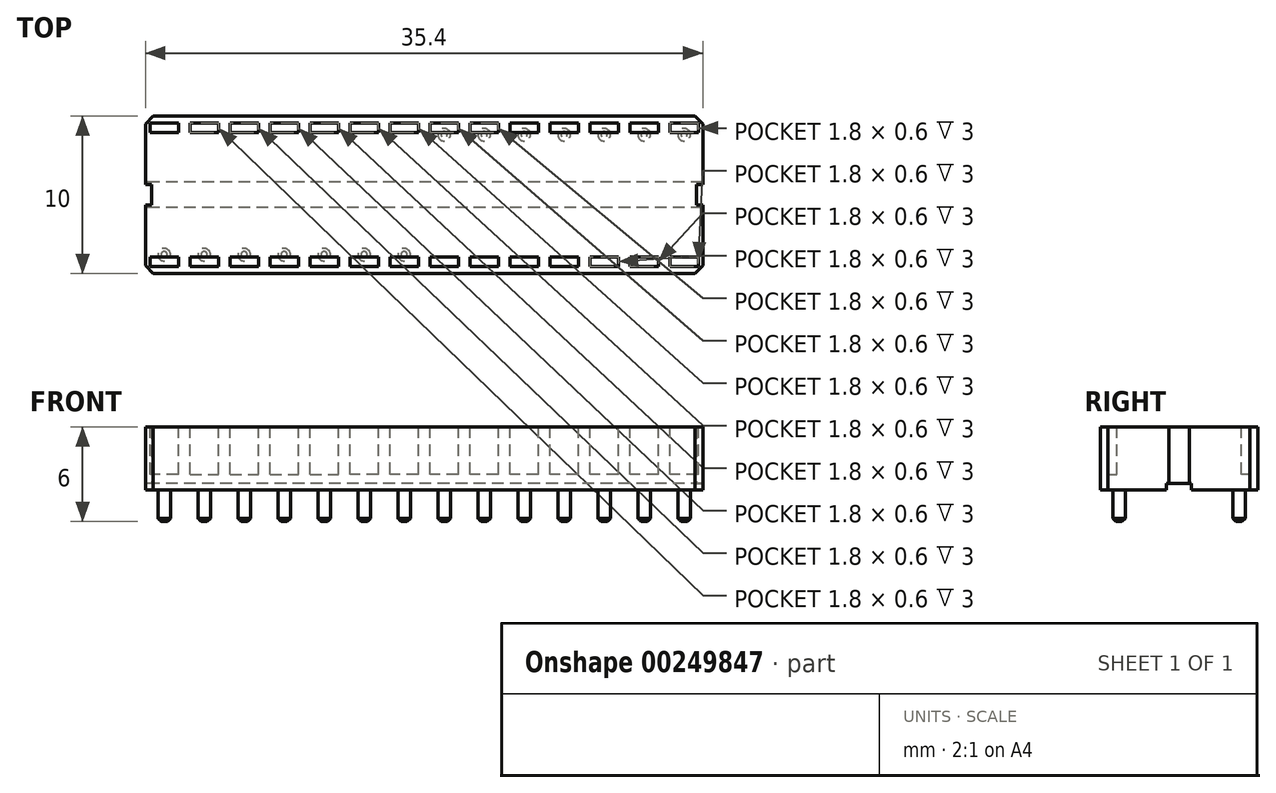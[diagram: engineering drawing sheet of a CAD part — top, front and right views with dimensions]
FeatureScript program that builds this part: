
annotation { "Feature Type Name" : "Feature", "Feature Type Description" : "" }
export const myFeature = defineFeature(function(context is Context, id is Id, definition is map)
    precondition{}
    {
        {
            var Q0;
            Q0=qCreatedBy(makeId("Top.planeOp"),FACE);
            var sketch = newSketch(context, id + "F0", { "sketchPlane" : qUnion([Q0])});
            skLineSegment(sketch, "E0.bottom", {"start": v(0, 0) * mm, "end": v(35.4, 0) * mm});
            skLineSegment(sketch, "E0.top", {"start": v(0, 10) * mm, "end": v(35.4, 10) * mm});
            skLineSegment(sketch, "E0.left", {"start": v(0, 0) * mm, "end": v(0, 10) * mm});
            skLineSegment(sketch, "E0.right", {"start": v(35.4, 0) * mm, "end": v(35.4, 10) * mm});
            skSolve(sketch);
        }
        {
            var Q0;
            Q0=makeQuery(id+"F0.imprint","IMPRINT",FACE,{"disambiguationData":[TD([[makeQuery(id+"F0.imprint","IMPRINT",EDGE,{"derivedFrom":sQuery(id+"F0.wireOp",EDGE,"E0.bottom")}),1.0]])]});
            extrude(context, id + "F1", {"entities" : qUnion([Q0]), "depth" : 8.6 * mm});
        }
        {
            var Q0;
            Q0=makeQuery(id+"F1.opExtrude","CAP_FACE",FACE,{"disambiguationData":[OSD([sQuery(id+"F0.wireOp",EDGE,"E0.bottom"),sQuery(id+"F0.wireOp",EDGE,"E0.top"),sQuery(id+"F0.wireOp",EDGE,"E0.left"),sQuery(id+"F0.wireOp",EDGE,"E0.right")])],"isStart":true});
            var sketch = newSketch(context, id + "F2", { "sketchPlane" : qUnion([Q0])});
            skLineSegment(sketch, "E1", {"start": v(0, -5) * mm, "end": v(35.4, -5) * mm, "construction": true});
            skLineSegment(sketch, "E2", {"start": v(17.7, 0) * mm, "end": v(17.7, -10) * mm, "construction": true});
            skLineSegment(sketch, "E3", {"start": v(0, -1.19) * mm, "end": v(35.4, -1.19) * mm, "construction": true});
            skCircle(sketch, "E4", {"center": v(16.43, -1.19) * mm, "radius": 0.4 * mm});
            skCircle(sketch, "E5.1.0.0", {"center": v(13.89, -1.19) * mm, "radius": 0.4 * mm});
            skCircle(sketch, "E5.2.0.0", {"center": v(11.35, -1.19) * mm, "radius": 0.4 * mm});
            skCircle(sketch, "E5.3.0.0", {"center": v(8.8, -1.19) * mm, "radius": 0.4 * mm});
            skCircle(sketch, "E5.4.0.0", {"center": v(6.27, -1.19) * mm, "radius": 0.4 * mm});
            skCircle(sketch, "E5.5.0.0", {"center": v(3.73, -1.19) * mm, "radius": 0.4 * mm});
            skCircle(sketch, "E5.6.0.0", {"center": v(1.19, -1.19) * mm, "radius": 0.4 * mm});
            skLineSegment(sketch, "E5.direction1", {"start": v(16.43, -1.19) * mm, "end": v(13.89, -1.19) * mm, "construction": true});
            skCircle(sketch, "E6.MirrorC", {"center": v(1.19, -8.8) * mm, "radius": 0.4 * mm});
            skCircle(sketch, "E7.MirrorC", {"center": v(3.73, -8.8) * mm, "radius": 0.4 * mm});
            skCircle(sketch, "E8.MirrorC", {"center": v(6.27, -8.8) * mm, "radius": 0.4 * mm});
            skCircle(sketch, "E9.MirrorC", {"center": v(8.8, -8.8) * mm, "radius": 0.4 * mm});
            skCircle(sketch, "E10.MirrorC", {"center": v(11.35, -8.8) * mm, "radius": 0.4 * mm});
            skCircle(sketch, "E11.MirrorC", {"center": v(13.89, -8.8) * mm, "radius": 0.4 * mm});
            skCircle(sketch, "E12.MirrorC", {"center": v(16.43, -8.8) * mm, "radius": 0.4 * mm});
            skCircle(sketch, "E13.MirrorC", {"center": v(34.2, -1.19) * mm, "radius": 0.4 * mm});
            skCircle(sketch, "E14.MirrorC", {"center": v(31.67, -1.19) * mm, "radius": 0.4 * mm});
            skCircle(sketch, "E15.MirrorC", {"center": v(29.13, -1.19) * mm, "radius": 0.4 * mm});
            skCircle(sketch, "E16.MirrorC", {"center": v(26.6, -1.19) * mm, "radius": 0.4 * mm});
            skCircle(sketch, "E17.MirrorC", {"center": v(24.05, -1.19) * mm, "radius": 0.4 * mm});
            skCircle(sketch, "E18.MirrorC", {"center": v(21.51, -1.19) * mm, "radius": 0.4 * mm});
            skCircle(sketch, "E19.MirrorC", {"center": v(18.97, -1.19) * mm, "radius": 0.4 * mm});
            skCircle(sketch, "E20.MirrorC", {"center": v(18.97, -8.8) * mm, "radius": 0.4 * mm});
            skCircle(sketch, "E21.MirrorC", {"center": v(21.51, -8.8) * mm, "radius": 0.4 * mm});
            skCircle(sketch, "E22.MirrorC", {"center": v(24.05, -8.8) * mm, "radius": 0.4 * mm});
            skCircle(sketch, "E23.MirrorC", {"center": v(26.6, -8.8) * mm, "radius": 0.4 * mm});
            skCircle(sketch, "E24.MirrorC", {"center": v(29.13, -8.8) * mm, "radius": 0.4 * mm});
            skCircle(sketch, "E25.MirrorC", {"center": v(31.67, -8.8) * mm, "radius": 0.4 * mm});
            skCircle(sketch, "E26.MirrorC", {"center": v(34.2, -8.8) * mm, "radius": 0.4 * mm});
            skSolve(sketch);
        }
        {
            var Q0;
            Q0=makeQuery(id+"F2.imprint","IMPRINT",FACE,{"disambiguationData":[TD([[makeQuery(id+"F2.imprint","IMPRINT",EDGE,{"derivedFrom":sQuery(id+"F2.wireOp",EDGE,"E8.MirrorC")}),-1.0]])]});
            var Q1;
            Q1=makeQuery(id+"F2.imprint","IMPRINT",FACE,{"disambiguationData":[TD([[makeQuery(id+"F2.imprint","IMPRINT",EDGE,{"derivedFrom":sQuery(id+"F2.wireOp",EDGE,"E7.MirrorC")}),-1.0]])]});
            var Q2;
            Q2=makeQuery(id+"F2.imprint","IMPRINT",FACE,{"disambiguationData":[TD([[makeQuery(id+"F2.imprint","IMPRINT",EDGE,{"derivedFrom":sQuery(id+"F2.wireOp",EDGE,"E6.MirrorC")}),-1.0]])]});
            var Q3;
            Q3=makeQuery(id+"F2.imprint","IMPRINT",FACE,{"disambiguationData":[TD([[makeQuery(id+"F2.imprint","IMPRINT",EDGE,{"derivedFrom":sQuery(id+"F2.wireOp",EDGE,"E5.6.0.0")}),1.0]])]});
            var Q4;
            Q4=makeQuery(id+"F2.imprint","IMPRINT",FACE,{"disambiguationData":[TD([[makeQuery(id+"F2.imprint","IMPRINT",EDGE,{"derivedFrom":sQuery(id+"F2.wireOp",EDGE,"E5.5.0.0")}),1.0]])]});
            var Q5;
            Q5=makeQuery(id+"F2.imprint","IMPRINT",FACE,{"disambiguationData":[TD([[makeQuery(id+"F2.imprint","IMPRINT",EDGE,{"derivedFrom":sQuery(id+"F2.wireOp",EDGE,"E5.4.0.0")}),1.0]])]});
            var Q6;
            Q6=makeQuery(id+"F2.imprint","IMPRINT",FACE,{"disambiguationData":[TD([[makeQuery(id+"F2.imprint","IMPRINT",EDGE,{"derivedFrom":sQuery(id+"F2.wireOp",EDGE,"E5.3.0.0")}),1.0]])]});
            var Q7;
            Q7=makeQuery(id+"F2.imprint","IMPRINT",FACE,{"disambiguationData":[TD([[makeQuery(id+"F2.imprint","IMPRINT",EDGE,{"derivedFrom":sQuery(id+"F2.wireOp",EDGE,"E9.MirrorC")}),-1.0]])]});
            var Q8;
            Q8=makeQuery(id+"F2.imprint","IMPRINT",FACE,{"disambiguationData":[TD([[makeQuery(id+"F2.imprint","IMPRINT",EDGE,{"derivedFrom":sQuery(id+"F2.wireOp",EDGE,"E5.2.0.0")}),1.0]])]});
            var Q9;
            Q9=makeQuery(id+"F2.imprint","IMPRINT",FACE,{"disambiguationData":[TD([[makeQuery(id+"F2.imprint","IMPRINT",EDGE,{"derivedFrom":sQuery(id+"F2.wireOp",EDGE,"E5.1.0.0")}),1.0]])]});
            var Q10;
            Q10=makeQuery(id+"F2.imprint","IMPRINT",FACE,{"disambiguationData":[TD([[makeQuery(id+"F2.imprint","IMPRINT",EDGE,{"derivedFrom":sQuery(id+"F2.wireOp",EDGE,"E10.MirrorC")}),-1.0]])]});
            var Q11;
            Q11=makeQuery(id+"F2.imprint","IMPRINT",FACE,{"disambiguationData":[TD([[makeQuery(id+"F2.imprint","IMPRINT",EDGE,{"derivedFrom":sQuery(id+"F2.wireOp",EDGE,"E11.MirrorC")}),-1.0]])]});
            var Q12;
            Q12=makeQuery(id+"F2.imprint","IMPRINT",FACE,{"disambiguationData":[TD([[makeQuery(id+"F2.imprint","IMPRINT",EDGE,{"derivedFrom":sQuery(id+"F2.wireOp",EDGE,"E4")}),1.0]])]});
            var Q13;
            Q13=makeQuery(id+"F2.imprint","IMPRINT",FACE,{"disambiguationData":[TD([[makeQuery(id+"F2.imprint","IMPRINT",EDGE,{"derivedFrom":sQuery(id+"F2.wireOp",EDGE,"E12.MirrorC")}),-1.0]])]});
            var Q14;
            Q14=makeQuery(id+"F2.imprint","IMPRINT",FACE,{"disambiguationData":[TD([[makeQuery(id+"F2.imprint","IMPRINT",EDGE,{"derivedFrom":sQuery(id+"F2.wireOp",EDGE,"E19.MirrorC")}),-1.0]])]});
            var Q15;
            Q15=makeQuery(id+"F2.imprint","IMPRINT",FACE,{"disambiguationData":[TD([[makeQuery(id+"F2.imprint","IMPRINT",EDGE,{"derivedFrom":sQuery(id+"F2.wireOp",EDGE,"E18.MirrorC")}),-1.0]])]});
            var Q16;
            Q16=makeQuery(id+"F2.imprint","IMPRINT",FACE,{"disambiguationData":[TD([[makeQuery(id+"F2.imprint","IMPRINT",EDGE,{"derivedFrom":sQuery(id+"F2.wireOp",EDGE,"E20.MirrorC")}),1.0]])]});
            var Q17;
            Q17=makeQuery(id+"F2.imprint","IMPRINT",FACE,{"disambiguationData":[TD([[makeQuery(id+"F2.imprint","IMPRINT",EDGE,{"derivedFrom":sQuery(id+"F2.wireOp",EDGE,"E21.MirrorC")}),1.0]])]});
            var Q18;
            Q18=makeQuery(id+"F2.imprint","IMPRINT",FACE,{"disambiguationData":[TD([[makeQuery(id+"F2.imprint","IMPRINT",EDGE,{"derivedFrom":sQuery(id+"F2.wireOp",EDGE,"E22.MirrorC")}),1.0]])]});
            var Q19;
            Q19=makeQuery(id+"F2.imprint","IMPRINT",FACE,{"disambiguationData":[TD([[makeQuery(id+"F2.imprint","IMPRINT",EDGE,{"derivedFrom":sQuery(id+"F2.wireOp",EDGE,"E17.MirrorC")}),-1.0]])]});
            var Q20;
            Q20=makeQuery(id+"F2.imprint","IMPRINT",FACE,{"disambiguationData":[TD([[makeQuery(id+"F2.imprint","IMPRINT",EDGE,{"derivedFrom":sQuery(id+"F2.wireOp",EDGE,"E23.MirrorC")}),1.0]])]});
            var Q21;
            Q21=makeQuery(id+"F2.imprint","IMPRINT",FACE,{"disambiguationData":[TD([[makeQuery(id+"F2.imprint","IMPRINT",EDGE,{"derivedFrom":sQuery(id+"F2.wireOp",EDGE,"E16.MirrorC")}),-1.0]])]});
            var Q22;
            Q22=makeQuery(id+"F2.imprint","IMPRINT",FACE,{"disambiguationData":[TD([[makeQuery(id+"F2.imprint","IMPRINT",EDGE,{"derivedFrom":sQuery(id+"F2.wireOp",EDGE,"E15.MirrorC")}),-1.0]])]});
            var Q23;
            Q23=makeQuery(id+"F2.imprint","IMPRINT",FACE,{"disambiguationData":[TD([[makeQuery(id+"F2.imprint","IMPRINT",EDGE,{"derivedFrom":sQuery(id+"F2.wireOp",EDGE,"E24.MirrorC")}),1.0]])]});
            var Q24;
            Q24=makeQuery(id+"F2.imprint","IMPRINT",FACE,{"disambiguationData":[TD([[makeQuery(id+"F2.imprint","IMPRINT",EDGE,{"derivedFrom":sQuery(id+"F2.wireOp",EDGE,"E14.MirrorC")}),-1.0]])]});
            var Q25;
            Q25=makeQuery(id+"F2.imprint","IMPRINT",FACE,{"disambiguationData":[TD([[makeQuery(id+"F2.imprint","IMPRINT",EDGE,{"derivedFrom":sQuery(id+"F2.wireOp",EDGE,"E25.MirrorC")}),1.0]])]});
            var Q26;
            Q26=makeQuery(id+"F2.imprint","IMPRINT",FACE,{"disambiguationData":[TD([[makeQuery(id+"F2.imprint","IMPRINT",EDGE,{"derivedFrom":sQuery(id+"F2.wireOp",EDGE,"E13.MirrorC")}),-1.0]])]});
            var Q27;
            Q27=makeQuery(id+"F2.imprint","IMPRINT",FACE,{"disambiguationData":[TD([[makeQuery(id+"F2.imprint","IMPRINT",EDGE,{"derivedFrom":sQuery(id+"F2.wireOp",EDGE,"E26.MirrorC")}),1.0]])]});
            extrude(context, id + "F3", {"entities" : qUnion([Q0, Q1, Q2, Q3, Q4, Q5, Q6, Q7, Q8, Q9, Q10, Q11, Q12, Q13, Q14, Q15, Q16, Q17, Q18, Q19, Q20, Q21, Q22, Q23, Q24, Q25, Q26, Q27]), "operationType" : NewBodyOperationType.ADD, "depth" : 2 * mm});
        }
        {
            var Q0;
            Q0=makeQuery(id+"F3.opExtrude","CAP_EDGE",EDGE,{"disambiguationData":[OSD([sQuery(id+"F2.wireOp",EDGE,"E5.6.0.0")])],"isStart":false});
            var Q1;
            Q1=makeQuery(id+"F3.opExtrude","CAP_EDGE",EDGE,{"disambiguationData":[OSD([sQuery(id+"F2.wireOp",EDGE,"E5.5.0.0")])],"isStart":false});
            var Q2;
            Q2=makeQuery(id+"F3.opExtrude","CAP_EDGE",EDGE,{"disambiguationData":[OSD([sQuery(id+"F2.wireOp",EDGE,"E5.4.0.0")])],"isStart":false});
            var Q3;
            Q3=makeQuery(id+"F3.opExtrude","CAP_EDGE",EDGE,{"disambiguationData":[OSD([sQuery(id+"F2.wireOp",EDGE,"E5.3.0.0")])],"isStart":false});
            var Q4;
            Q4=makeQuery(id+"F3.opExtrude","CAP_EDGE",EDGE,{"disambiguationData":[OSD([sQuery(id+"F2.wireOp",EDGE,"E5.2.0.0")])],"isStart":false});
            var Q5;
            Q5=makeQuery(id+"F3.opExtrude","CAP_EDGE",EDGE,{"disambiguationData":[OSD([sQuery(id+"F2.wireOp",EDGE,"E5.1.0.0")])],"isStart":false});
            var Q6;
            Q6=makeQuery(id+"F3.opExtrude","CAP_EDGE",EDGE,{"disambiguationData":[OSD([sQuery(id+"F2.wireOp",EDGE,"E4")])],"isStart":false});
            var Q7;
            Q7=makeQuery(id+"F3.opExtrude","CAP_EDGE",EDGE,{"disambiguationData":[OSD([sQuery(id+"F2.wireOp",EDGE,"E6.MirrorC")])],"isStart":false});
            var Q8;
            Q8=makeQuery(id+"F3.opExtrude","CAP_EDGE",EDGE,{"disambiguationData":[OSD([sQuery(id+"F2.wireOp",EDGE,"E7.MirrorC")])],"isStart":false});
            var Q9;
            Q9=makeQuery(id+"F3.opExtrude","CAP_EDGE",EDGE,{"disambiguationData":[OSD([sQuery(id+"F2.wireOp",EDGE,"E8.MirrorC")])],"isStart":false});
            var Q10;
            Q10=makeQuery(id+"F3.opExtrude","CAP_EDGE",EDGE,{"disambiguationData":[OSD([sQuery(id+"F2.wireOp",EDGE,"E9.MirrorC")])],"isStart":false});
            var Q11;
            Q11=makeQuery(id+"F3.opExtrude","CAP_EDGE",EDGE,{"disambiguationData":[OSD([sQuery(id+"F2.wireOp",EDGE,"E10.MirrorC")])],"isStart":false});
            var Q12;
            Q12=makeQuery(id+"F3.opExtrude","CAP_EDGE",EDGE,{"disambiguationData":[OSD([sQuery(id+"F2.wireOp",EDGE,"E11.MirrorC")])],"isStart":false});
            var Q13;
            Q13=makeQuery(id+"F3.opExtrude","CAP_EDGE",EDGE,{"disambiguationData":[OSD([sQuery(id+"F2.wireOp",EDGE,"E12.MirrorC")])],"isStart":false});
            var Q14;
            Q14=makeQuery(id+"F3.opExtrude","CAP_EDGE",EDGE,{"disambiguationData":[OSD([sQuery(id+"F2.wireOp",EDGE,"E20.MirrorC")])],"isStart":false});
            var Q15;
            Q15=makeQuery(id+"F3.opExtrude","CAP_EDGE",EDGE,{"disambiguationData":[OSD([sQuery(id+"F2.wireOp",EDGE,"E19.MirrorC")])],"isStart":false});
            var Q16;
            Q16=makeQuery(id+"F3.opExtrude","CAP_EDGE",EDGE,{"disambiguationData":[OSD([sQuery(id+"F2.wireOp",EDGE,"E21.MirrorC")])],"isStart":false});
            var Q17;
            Q17=makeQuery(id+"F3.opExtrude","CAP_EDGE",EDGE,{"disambiguationData":[OSD([sQuery(id+"F2.wireOp",EDGE,"E22.MirrorC")])],"isStart":false});
            var Q18;
            Q18=makeQuery(id+"F3.opExtrude","CAP_EDGE",EDGE,{"disambiguationData":[OSD([sQuery(id+"F2.wireOp",EDGE,"E18.MirrorC")])],"isStart":false});
            var Q19;
            Q19=makeQuery(id+"F3.opExtrude","CAP_EDGE",EDGE,{"disambiguationData":[OSD([sQuery(id+"F2.wireOp",EDGE,"E17.MirrorC")])],"isStart":false});
            var Q20;
            Q20=makeQuery(id+"F3.opExtrude","CAP_EDGE",EDGE,{"disambiguationData":[OSD([sQuery(id+"F2.wireOp",EDGE,"E23.MirrorC")])],"isStart":false});
            var Q21;
            Q21=makeQuery(id+"F3.opExtrude","CAP_EDGE",EDGE,{"disambiguationData":[OSD([sQuery(id+"F2.wireOp",EDGE,"E24.MirrorC")])],"isStart":false});
            var Q22;
            Q22=makeQuery(id+"F3.opExtrude","CAP_EDGE",EDGE,{"disambiguationData":[OSD([sQuery(id+"F2.wireOp",EDGE,"E16.MirrorC")])],"isStart":false});
            var Q23;
            Q23=makeQuery(id+"F3.opExtrude","CAP_EDGE",EDGE,{"disambiguationData":[OSD([sQuery(id+"F2.wireOp",EDGE,"E15.MirrorC")])],"isStart":false});
            var Q24;
            Q24=makeQuery(id+"F3.opExtrude","CAP_EDGE",EDGE,{"disambiguationData":[OSD([sQuery(id+"F2.wireOp",EDGE,"E25.MirrorC")])],"isStart":false});
            var Q25;
            Q25=makeQuery(id+"F3.opExtrude","CAP_EDGE",EDGE,{"disambiguationData":[OSD([sQuery(id+"F2.wireOp",EDGE,"E26.MirrorC")])],"isStart":false});
            var Q26;
            Q26=makeQuery(id+"F3.opExtrude","CAP_EDGE",EDGE,{"disambiguationData":[OSD([sQuery(id+"F2.wireOp",EDGE,"E14.MirrorC")])],"isStart":false});
            var Q27;
            Q27=makeQuery(id+"F3.opExtrude","CAP_EDGE",EDGE,{"disambiguationData":[OSD([sQuery(id+"F2.wireOp",EDGE,"E13.MirrorC")])],"isStart":false});
            chamfer(context, id + "F4", {"entities" : qUnion([Q0, Q1, Q2, Q3, Q4, Q5, Q6, Q7, Q8, Q9, Q10, Q11, Q12, Q13, Q14, Q15, Q16, Q17, Q18, Q19, Q20, Q21, Q22, Q23, Q24, Q25, Q26, Q27]), "width" : 0.2 * mm, "tangentPropagation" : true});
        }
        {
            var Q0;
            Q0=makeQuery(id+"F1.opExtrude","SWEPT_EDGE",EDGE,{"disambiguationData":[OSD([sQuery(id+"F0.wireOp",EDGE,"E0.bottom"),sQuery(id+"F0.wireOp",EDGE,"E0.left")])]});
            var Q1;
            Q1=makeQuery(id+"F1.opExtrude","SWEPT_EDGE",EDGE,{"disambiguationData":[OSD([sQuery(id+"F0.wireOp",EDGE,"E0.top"),sQuery(id+"F0.wireOp",EDGE,"E0.left")])]});
            var Q2;
            Q2=makeQuery(id+"F1.opExtrude","SWEPT_EDGE",EDGE,{"disambiguationData":[OSD([sQuery(id+"F0.wireOp",EDGE,"E0.bottom"),sQuery(id+"F0.wireOp",EDGE,"E0.right")])]});
            var Q3;
            Q3=makeQuery(id+"F1.opExtrude","SWEPT_EDGE",EDGE,{"disambiguationData":[OSD([sQuery(id+"F0.wireOp",EDGE,"E0.top"),sQuery(id+"F0.wireOp",EDGE,"E0.right")])]});
            chamfer(context, id + "F5", {"entities" : qUnion([Q0, Q1, Q2, Q3]), "width" : 0.5 * mm, "tangentPropagation" : true});
        }
        {
            var Q0;
            Q0=makeQuery(id+"F1.opExtrude","CAP_FACE",FACE,{"disambiguationData":[OSD([sQuery(id+"F0.wireOp",EDGE,"E0.bottom"),sQuery(id+"F0.wireOp",EDGE,"E0.top"),sQuery(id+"F0.wireOp",EDGE,"E0.left"),sQuery(id+"F0.wireOp",EDGE,"E0.right")])],"isStart":false});
            var sketch = newSketch(context, id + "F6", { "sketchPlane" : qUnion([Q0])});
            skLineSegment(sketch, "E27", {"start": v(0.5, 0) * mm, "end": v(34.9, 0) * mm});
            skLineSegment(sketch, "E28", {"start": v(34.9, 0) * mm, "end": v(35.4, 0.5) * mm});
            skLineSegment(sketch, "E29", {"start": v(35.4, 0.5) * mm, "end": v(35.4, 9.5) * mm});
            skLineSegment(sketch, "E30", {"start": v(35.4, 9.5) * mm, "end": v(34.9, 10) * mm});
            skLineSegment(sketch, "E31", {"start": v(34.9, 10) * mm, "end": v(0.5, 10) * mm});
            skLineSegment(sketch, "E32", {"start": v(0.5, 10) * mm, "end": v(0, 9.5) * mm});
            skLineSegment(sketch, "E33", {"start": v(0, 9.5) * mm, "end": v(0, 0.5) * mm});
            skLineSegment(sketch, "E34", {"start": v(0, 0.5) * mm, "end": v(0.5, 0) * mm});
            skSolve(sketch);
        }
        {
            var Q0;
            Q0=makeQuery(id+"F6.imprint","IMPRINT",FACE,{"disambiguationData":[TD([[makeQuery(id+"F6.imprint","IMPRINT",EDGE,{"derivedFrom":sQuery(id+"F6.wireOp",EDGE,"E27")}),1.0]])]});
            extrude(context, id + "F7", {"entities" : qUnion([Q0]), "operationType" : NewBodyOperationType.REMOVE, "oppositeDirection" : true, "depth" : 4.6 * mm});
        }
        {
            var Q0;
            Q0=makeQuery(id+"F1.opExtrude","SWEPT_FACE",FACE,{"disambiguationData":[OSD([sQuery(id+"F0.wireOp",EDGE,"E0.right")])]});
            var sketch = newSketch(context, id + "F8", { "sketchPlane" : qUnion([Q0])});
            skLineSegment(sketch, "E35", {"start": v(5, 4) * mm, "end": v(5, 0) * mm, "construction": true});
            skLineSegment(sketch, "E36.bottom", {"start": v(4.35, 4) * mm, "end": v(5.65, 4) * mm});
            skLineSegment(sketch, "E36.top", {"start": v(4.35, 0) * mm, "end": v(5.65, 0) * mm});
            skLineSegment(sketch, "E36.left", {"start": v(4.35, 4) * mm, "end": v(4.35, 0) * mm});
            skLineSegment(sketch, "E36.right", {"start": v(5.65, 4) * mm, "end": v(5.65, 0) * mm});
            skSolve(sketch);
        }
        {
            var Q0;
            Q0 = qSketchRegion(id + "F8", true);
            extrude(context, id + "F9", {"entities" : qUnion([Q0]), "operationType" : NewBodyOperationType.REMOVE, "oppositeDirection" : true, "depth" : 0.4 * mm});
        }
        {
            var Q0;
            Q0=makeQuery(id+"F1.opExtrude","SWEPT_FACE",FACE,{"disambiguationData":[OSD([sQuery(id+"F0.wireOp",EDGE,"E0.left")])]});
            var sketch = newSketch(context, id + "F10", { "sketchPlane" : qUnion([Q0])});
            skLineSegment(sketch, "E37", {"start": v(-5, 4) * mm, "end": v(-5, 0) * mm, "construction": true});
            skLineSegment(sketch, "E38.bottom", {"start": v(-5.65, 4) * mm, "end": v(-4.35, 4) * mm});
            skLineSegment(sketch, "E38.top", {"start": v(-5.65, 0) * mm, "end": v(-4.35, 0) * mm});
            skLineSegment(sketch, "E38.left", {"start": v(-5.65, 4) * mm, "end": v(-5.65, 0) * mm});
            skLineSegment(sketch, "E38.right", {"start": v(-4.35, 4) * mm, "end": v(-4.35, 0) * mm});
            skSolve(sketch);
        }
        {
            var Q0;
            Q0 = qSketchRegion(id + "F10", true);
            extrude(context, id + "F11", {"entities" : qUnion([Q0]), "operationType" : NewBodyOperationType.REMOVE, "oppositeDirection" : true, "depth" : 0.4 * mm});
        }
        {
            var Q0;
            Q0=makeQuery(id+"F1.opExtrude","CAP_FACE",FACE,{"disambiguationData":[OSD([sQuery(id+"F0.wireOp",EDGE,"E0.bottom"),sQuery(id+"F0.wireOp",EDGE,"E0.top"),sQuery(id+"F0.wireOp",EDGE,"E0.left"),sQuery(id+"F0.wireOp",EDGE,"E0.right")])],"isStart":true});
            var sketch = newSketch(context, id + "F12", { "sketchPlane" : qUnion([Q0])});
            skLineSegment(sketch, "E39", {"start": v(0.4, -5) * mm, "end": v(35, -5) * mm, "construction": true});
            skLineSegment(sketch, "E40.bottom", {"start": v(35.4, -5.8) * mm, "end": v(0, -5.8) * mm});
            skLineSegment(sketch, "E40.top", {"start": v(35.4, -4.2) * mm, "end": v(0, -4.2) * mm});
            skLineSegment(sketch, "E40.left", {"start": v(35.4, -5.8) * mm, "end": v(35.4, -4.2) * mm});
            skLineSegment(sketch, "E40.right", {"start": v(0, -5.8) * mm, "end": v(0, -4.2) * mm});
            skSolve(sketch);
        }
        {
            var Q0;
            Q0 = qSketchRegion(id + "F12", true);
            extrude(context, id + "F13", {"entities" : qUnion([Q0]), "operationType" : NewBodyOperationType.REMOVE, "oppositeDirection" : true, "depth" : 0.4 * mm});
        }
        {
            var Q0;
            Q0=makeQuery(id+"F7.boolean.opBoolean","COPY",FACE,{"derivedFrom":makeQuery(id+"F7.opExtrude","CAP_FACE",FACE,{"disambiguationData":[OSD([sQuery(id+"F6.wireOp",EDGE,"E27"),sQuery(id+"F6.wireOp",EDGE,"E28"),sQuery(id+"F6.wireOp",EDGE,"E29"),sQuery(id+"F6.wireOp",EDGE,"E30"),sQuery(id+"F6.wireOp",EDGE,"E31"),sQuery(id+"F6.wireOp",EDGE,"E32"),sQuery(id+"F6.wireOp",EDGE,"E33"),sQuery(id+"F6.wireOp",EDGE,"E34")])],"isStart":false})});
            var sketch = newSketch(context, id + "F14", { "sketchPlane" : qUnion([Q0])});
            skLineSegment(sketch, "E41", {"start": v(35, 5) * mm, "end": v(0.4, 5) * mm, "construction": true});
            skLineSegment(sketch, "E42.bottom", {"start": v(33.23, 8.5) * mm, "end": v(2.45, 8.5) * mm, "construction": true});
            skLineSegment(sketch, "E42.top", {"start": v(33.23, 1.5) * mm, "end": v(2.45, 1.5) * mm, "construction": true});
            skLineSegment(sketch, "E42.left", {"start": v(33.23, 8.5) * mm, "end": v(33.23, 1.5) * mm, "construction": true});
            skLineSegment(sketch, "E42.right", {"start": v(2.45, 8.5) * mm, "end": v(2.45, 1.5) * mm, "construction": true});
            skLineSegment(sketch, "E43", {"start": v(17.7, 10) * mm, "end": v(17.7, 0) * mm, "construction": true});
            skLineSegment(sketch, "E44.bottom", {"start": v(17.33, 9.55) * mm, "end": v(15.53, 9.55) * mm});
            skLineSegment(sketch, "E44.top", {"start": v(17.33, 8.95) * mm, "end": v(15.53, 8.95) * mm});
            skLineSegment(sketch, "E44.left", {"start": v(17.33, 9.55) * mm, "end": v(17.33, 8.95) * mm});
            skLineSegment(sketch, "E44.right", {"start": v(15.53, 9.55) * mm, "end": v(15.53, 8.95) * mm});
            skLineSegment(sketch, "E45.1.0.0", {"start": v(19.87, 9.55) * mm, "end": v(18.07, 9.55) * mm});
            skLineSegment(sketch, "E45.1.0.1", {"start": v(19.87, 9.55) * mm, "end": v(19.87, 8.95) * mm});
            skLineSegment(sketch, "E45.1.0.2", {"start": v(19.87, 8.95) * mm, "end": v(18.07, 8.95) * mm});
            skLineSegment(sketch, "E45.1.0.3", {"start": v(18.07, 9.55) * mm, "end": v(18.07, 8.95) * mm});
            skLineSegment(sketch, "E45.2.0.0", {"start": v(22.41, 9.55) * mm, "end": v(20.61, 9.55) * mm});
            skLineSegment(sketch, "E45.2.0.1", {"start": v(22.41, 9.55) * mm, "end": v(22.41, 8.95) * mm});
            skLineSegment(sketch, "E45.2.0.2", {"start": v(22.41, 8.95) * mm, "end": v(20.61, 8.95) * mm});
            skLineSegment(sketch, "E45.2.0.3", {"start": v(20.61, 9.55) * mm, "end": v(20.61, 8.95) * mm});
            skLineSegment(sketch, "E45.3.0.0", {"start": v(24.95, 9.55) * mm, "end": v(23.15, 9.55) * mm});
            skLineSegment(sketch, "E45.3.0.1", {"start": v(24.95, 9.55) * mm, "end": v(24.95, 8.95) * mm});
            skLineSegment(sketch, "E45.3.0.2", {"start": v(24.95, 8.95) * mm, "end": v(23.15, 8.95) * mm});
            skLineSegment(sketch, "E45.3.0.3", {"start": v(23.15, 9.55) * mm, "end": v(23.15, 8.95) * mm});
            skLineSegment(sketch, "E45.4.0.0", {"start": v(27.5, 9.55) * mm, "end": v(25.7, 9.55) * mm});
            skLineSegment(sketch, "E45.4.0.1", {"start": v(27.5, 9.55) * mm, "end": v(27.5, 8.95) * mm});
            skLineSegment(sketch, "E45.4.0.2", {"start": v(27.5, 8.95) * mm, "end": v(25.7, 8.95) * mm});
            skLineSegment(sketch, "E45.4.0.3", {"start": v(25.7, 9.55) * mm, "end": v(25.7, 8.95) * mm});
            skLineSegment(sketch, "E45.5.0.0", {"start": v(30.03, 9.55) * mm, "end": v(28.23, 9.55) * mm});
            skLineSegment(sketch, "E45.5.0.1", {"start": v(30.03, 9.55) * mm, "end": v(30.03, 8.95) * mm});
            skLineSegment(sketch, "E45.5.0.2", {"start": v(30.03, 8.95) * mm, "end": v(28.23, 8.95) * mm});
            skLineSegment(sketch, "E45.5.0.3", {"start": v(28.23, 9.55) * mm, "end": v(28.23, 8.95) * mm});
            skLineSegment(sketch, "E45.6.0.0", {"start": v(32.57, 9.55) * mm, "end": v(30.77, 9.55) * mm});
            skLineSegment(sketch, "E45.6.0.1", {"start": v(32.57, 9.55) * mm, "end": v(32.57, 8.95) * mm});
            skLineSegment(sketch, "E45.6.0.2", {"start": v(32.57, 8.95) * mm, "end": v(30.77, 8.95) * mm});
            skLineSegment(sketch, "E45.6.0.3", {"start": v(30.77, 9.55) * mm, "end": v(30.77, 8.95) * mm});
            skLineSegment(sketch, "E45.7.0.0", {"start": v(35.1, 9.55) * mm, "end": v(33.31, 9.55) * mm});
            skLineSegment(sketch, "E45.7.0.1", {"start": v(35.1, 9.55) * mm, "end": v(35.1, 8.95) * mm});
            skLineSegment(sketch, "E45.7.0.2", {"start": v(35.1, 8.95) * mm, "end": v(33.31, 8.95) * mm});
            skLineSegment(sketch, "E45.7.0.3", {"start": v(33.31, 9.55) * mm, "end": v(33.31, 8.95) * mm});
            skLineSegment(sketch, "E45.direction1", {"start": v(15.53, 9.55) * mm, "end": v(18.07, 9.55) * mm, "construction": true});
            skLineSegment(sketch, "E46.1.0.0", {"start": v(14.8, 8.95) * mm, "end": v(13, 8.95) * mm});
            skLineSegment(sketch, "E46.1.0.1", {"start": v(13, 9.55) * mm, "end": v(13, 8.95) * mm});
            skLineSegment(sketch, "E46.1.0.2", {"start": v(14.8, 9.55) * mm, "end": v(14.8, 8.95) * mm});
            skLineSegment(sketch, "E46.2.0.0", {"start": v(12.25, 8.95) * mm, "end": v(10.45, 8.95) * mm});
            skLineSegment(sketch, "E46.2.0.1", {"start": v(10.45, 9.55) * mm, "end": v(10.45, 8.95) * mm});
            skLineSegment(sketch, "E46.2.0.2", {"start": v(12.25, 9.55) * mm, "end": v(12.25, 8.95) * mm});
            skLineSegment(sketch, "E46.3.0.0", {"start": v(9.7, 8.95) * mm, "end": v(7.9, 8.95) * mm});
            skLineSegment(sketch, "E46.3.0.1", {"start": v(7.9, 9.55) * mm, "end": v(7.9, 8.95) * mm});
            skLineSegment(sketch, "E46.3.0.2", {"start": v(9.7, 9.55) * mm, "end": v(9.7, 8.95) * mm});
            skLineSegment(sketch, "E46.4.0.0", {"start": v(7.17, 8.95) * mm, "end": v(5.37, 8.95) * mm});
            skLineSegment(sketch, "E46.4.0.1", {"start": v(5.37, 9.55) * mm, "end": v(5.37, 8.95) * mm});
            skLineSegment(sketch, "E46.4.0.2", {"start": v(7.17, 9.55) * mm, "end": v(7.17, 8.95) * mm});
            skLineSegment(sketch, "E46.5.0.0", {"start": v(4.63, 8.95) * mm, "end": v(2.83, 8.95) * mm});
            skLineSegment(sketch, "E46.5.0.1", {"start": v(2.83, 9.55) * mm, "end": v(2.83, 8.95) * mm});
            skLineSegment(sketch, "E46.5.0.2", {"start": v(4.63, 9.55) * mm, "end": v(4.63, 8.95) * mm});
            skLineSegment(sketch, "E46.6.0.0", {"start": v(2.09, 8.95) * mm, "end": v(0.29, 8.95) * mm});
            skLineSegment(sketch, "E46.6.0.1", {"start": v(0.29, 9.55) * mm, "end": v(0.29, 8.95) * mm});
            skLineSegment(sketch, "E46.6.0.2", {"start": v(2.09, 9.55) * mm, "end": v(2.09, 8.95) * mm});
            skLineSegment(sketch, "E46.direction1", {"start": v(15.53, 8.95) * mm, "end": v(13, 8.95) * mm, "construction": true});
            skLineSegment(sketch, "E47", {"start": v(0.29, 9.55) * mm, "end": v(2.09, 9.55) * mm});
            skLineSegment(sketch, "E48", {"start": v(2.83, 9.55) * mm, "end": v(4.63, 9.55) * mm});
            skLineSegment(sketch, "E49", {"start": v(5.37, 9.55) * mm, "end": v(7.17, 9.55) * mm});
            skLineSegment(sketch, "E50", {"start": v(7.9, 9.55) * mm, "end": v(9.7, 9.55) * mm});
            skLineSegment(sketch, "E51", {"start": v(10.45, 9.55) * mm, "end": v(12.25, 9.55) * mm});
            skLineSegment(sketch, "E52", {"start": v(13, 9.55) * mm, "end": v(14.8, 9.55) * mm});
            skLineSegment(sketch, "E53.MirrorCS", {"start": v(2.09, 1.05) * mm, "end": v(0.29, 1.05) * mm});
            skLineSegment(sketch, "E54.MirrorCS", {"start": v(2.09, 0.45) * mm, "end": v(2.09, 1.05) * mm});
            skLineSegment(sketch, "E55.MirrorCS", {"start": v(0.29, 0.45) * mm, "end": v(2.09, 0.45) * mm});
            skLineSegment(sketch, "E56.MirrorCS", {"start": v(0.29, 0.45) * mm, "end": v(0.29, 1.05) * mm});
            skLineSegment(sketch, "E57.MirrorCS", {"start": v(2.83, 0.45) * mm, "end": v(2.83, 1.05) * mm});
            skLineSegment(sketch, "E58.MirrorCS", {"start": v(2.83, 0.45) * mm, "end": v(4.63, 0.45) * mm});
            skLineSegment(sketch, "E59.MirrorCS", {"start": v(4.63, 0.45) * mm, "end": v(4.63, 1.05) * mm});
            skLineSegment(sketch, "E60.MirrorCS", {"start": v(4.63, 1.05) * mm, "end": v(2.83, 1.05) * mm});
            skLineSegment(sketch, "E61.MirrorCS", {"start": v(5.37, 0.45) * mm, "end": v(5.37, 1.05) * mm});
            skLineSegment(sketch, "E62.MirrorCS", {"start": v(5.37, 0.45) * mm, "end": v(7.17, 0.45) * mm});
            skLineSegment(sketch, "E63.MirrorCS", {"start": v(7.17, 1.05) * mm, "end": v(5.37, 1.05) * mm});
            skLineSegment(sketch, "E64.MirrorCS", {"start": v(7.17, 0.45) * mm, "end": v(7.17, 1.05) * mm});
            skLineSegment(sketch, "E65.MirrorCS", {"start": v(7.9, 0.45) * mm, "end": v(7.9, 1.05) * mm});
            skLineSegment(sketch, "E66.MirrorCS", {"start": v(7.9, 0.45) * mm, "end": v(9.7, 0.45) * mm});
            skLineSegment(sketch, "E67.MirrorCS", {"start": v(9.7, 1.05) * mm, "end": v(7.9, 1.05) * mm});
            skLineSegment(sketch, "E68.MirrorCS", {"start": v(9.7, 0.45) * mm, "end": v(9.7, 1.05) * mm});
            skLineSegment(sketch, "E69.MirrorCS", {"start": v(12.25, 0.45) * mm, "end": v(12.25, 1.05) * mm});
            skLineSegment(sketch, "E70.MirrorCS", {"start": v(10.45, 0.45) * mm, "end": v(12.25, 0.45) * mm});
            skLineSegment(sketch, "E71.MirrorCS", {"start": v(10.45, 0.45) * mm, "end": v(10.45, 1.05) * mm});
            skLineSegment(sketch, "E72.MirrorCS", {"start": v(12.25, 1.05) * mm, "end": v(10.45, 1.05) * mm});
            skLineSegment(sketch, "E73.MirrorCS", {"start": v(14.8, 1.05) * mm, "end": v(13, 1.05) * mm});
            skLineSegment(sketch, "E74.MirrorCS", {"start": v(13, 0.45) * mm, "end": v(13, 1.05) * mm});
            skLineSegment(sketch, "E75.MirrorCS", {"start": v(15.53, 1.05) * mm, "end": v(13, 1.05) * mm, "construction": true});
            skLineSegment(sketch, "E76.MirrorCS", {"start": v(14.8, 0.45) * mm, "end": v(14.8, 1.05) * mm});
            skLineSegment(sketch, "E77.MirrorCS", {"start": v(13, 0.45) * mm, "end": v(14.8, 0.45) * mm});
            skLineSegment(sketch, "E78.MirrorCS", {"start": v(17.33, 0.45) * mm, "end": v(15.53, 0.45) * mm});
            skLineSegment(sketch, "E79.MirrorCS", {"start": v(17.33, 1.05) * mm, "end": v(15.53, 1.05) * mm});
            skLineSegment(sketch, "E80.MirrorCS", {"start": v(15.53, 0.45) * mm, "end": v(15.53, 1.05) * mm});
            skLineSegment(sketch, "E81.MirrorCS", {"start": v(17.33, 0.45) * mm, "end": v(17.33, 1.05) * mm});
            skLineSegment(sketch, "E82.MirrorCS", {"start": v(20.61, 0.45) * mm, "end": v(20.61, 1.05) * mm});
            skLineSegment(sketch, "E83.MirrorCS", {"start": v(24.95, 0.45) * mm, "end": v(23.15, 0.45) * mm});
            skLineSegment(sketch, "E84.MirrorCS", {"start": v(22.41, 1.05) * mm, "end": v(20.61, 1.05) * mm});
            skLineSegment(sketch, "E85.MirrorCS", {"start": v(24.95, 0.45) * mm, "end": v(24.95, 1.05) * mm});
            skLineSegment(sketch, "E86.MirrorCS", {"start": v(19.87, 1.05) * mm, "end": v(18.07, 1.05) * mm});
            skLineSegment(sketch, "E87.MirrorCS", {"start": v(19.87, 0.45) * mm, "end": v(19.87, 1.05) * mm});
            skLineSegment(sketch, "E88.MirrorCS", {"start": v(19.87, 0.45) * mm, "end": v(18.07, 0.45) * mm});
            skLineSegment(sketch, "E89.MirrorCS", {"start": v(23.15, 0.45) * mm, "end": v(23.15, 1.05) * mm});
            skLineSegment(sketch, "E90.MirrorCS", {"start": v(18.07, 0.45) * mm, "end": v(18.07, 1.05) * mm});
            skLineSegment(sketch, "E91.MirrorCS", {"start": v(22.41, 0.45) * mm, "end": v(20.61, 0.45) * mm});
            skLineSegment(sketch, "E92.MirrorCS", {"start": v(22.41, 0.45) * mm, "end": v(22.41, 1.05) * mm});
            skLineSegment(sketch, "E93.MirrorCS", {"start": v(24.95, 1.05) * mm, "end": v(23.15, 1.05) * mm});
            skLineSegment(sketch, "E94.MirrorCS", {"start": v(27.5, 1.05) * mm, "end": v(25.7, 1.05) * mm});
            skLineSegment(sketch, "E95.MirrorCS", {"start": v(30.77, 0.45) * mm, "end": v(30.77, 1.05) * mm});
            skLineSegment(sketch, "E96.MirrorCS", {"start": v(35.1, 0.45) * mm, "end": v(33.31, 0.45) * mm});
            skLineSegment(sketch, "E97.MirrorCS", {"start": v(27.5, 0.45) * mm, "end": v(27.5, 1.05) * mm});
            skLineSegment(sketch, "E98.MirrorCS", {"start": v(25.7, 0.45) * mm, "end": v(25.7, 1.05) * mm});
            skLineSegment(sketch, "E99.MirrorCS", {"start": v(35.1, 0.45) * mm, "end": v(35.1, 1.05) * mm});
            skLineSegment(sketch, "E100.MirrorCS", {"start": v(32.57, 1.05) * mm, "end": v(30.77, 1.05) * mm});
            skLineSegment(sketch, "E101.MirrorCS", {"start": v(30.03, 0.45) * mm, "end": v(28.23, 0.45) * mm});
            skLineSegment(sketch, "E102.MirrorCS", {"start": v(28.23, 0.45) * mm, "end": v(28.23, 1.05) * mm});
            skLineSegment(sketch, "E103.MirrorCS", {"start": v(35.1, 1.05) * mm, "end": v(33.31, 1.05) * mm});
            skLineSegment(sketch, "E104.MirrorCS", {"start": v(30.03, 1.05) * mm, "end": v(28.23, 1.05) * mm});
            skLineSegment(sketch, "E105.MirrorCS", {"start": v(27.5, 0.45) * mm, "end": v(25.7, 0.45) * mm});
            skLineSegment(sketch, "E106.MirrorCS", {"start": v(32.57, 0.45) * mm, "end": v(32.57, 1.05) * mm});
            skLineSegment(sketch, "E107.MirrorCS", {"start": v(30.03, 0.45) * mm, "end": v(30.03, 1.05) * mm});
            skLineSegment(sketch, "E108.MirrorCS", {"start": v(33.31, 0.45) * mm, "end": v(33.31, 1.05) * mm});
            skLineSegment(sketch, "E109.MirrorCS", {"start": v(32.57, 0.45) * mm, "end": v(30.77, 0.45) * mm});
            skSolve(sketch);
        }
        {
            var Q0;
            Q0=makeQuery(id+"F14.imprint","IMPRINT",FACE,{"disambiguationData":[TD([[makeQuery(id+"F14.imprint","IMPRINT",EDGE,{"derivedFrom":sQuery(id+"F14.wireOp",EDGE,"E46.6.0.0")}),-1.0]])]});
            var Q1;
            Q1=makeQuery(id+"F14.imprint","IMPRINT",FACE,{"disambiguationData":[TD([[makeQuery(id+"F14.imprint","IMPRINT",EDGE,{"derivedFrom":sQuery(id+"F14.wireOp",EDGE,"E46.5.0.0")}),-1.0]])]});
            var Q2;
            Q2=makeQuery(id+"F14.imprint","IMPRINT",FACE,{"disambiguationData":[TD([[makeQuery(id+"F14.imprint","IMPRINT",EDGE,{"derivedFrom":sQuery(id+"F14.wireOp",EDGE,"E46.4.0.0")}),-1.0]])]});
            var Q3;
            Q3=makeQuery(id+"F14.imprint","IMPRINT",FACE,{"disambiguationData":[TD([[makeQuery(id+"F14.imprint","IMPRINT",EDGE,{"derivedFrom":sQuery(id+"F14.wireOp",EDGE,"E46.3.0.0")}),-1.0]])]});
            var Q4;
            Q4=makeQuery(id+"F14.imprint","IMPRINT",FACE,{"disambiguationData":[TD([[makeQuery(id+"F14.imprint","IMPRINT",EDGE,{"derivedFrom":sQuery(id+"F14.wireOp",EDGE,"E46.2.0.0")}),-1.0]])]});
            var Q5;
            Q5=makeQuery(id+"F14.imprint","IMPRINT",FACE,{"disambiguationData":[TD([[makeQuery(id+"F14.imprint","IMPRINT",EDGE,{"derivedFrom":sQuery(id+"F14.wireOp",EDGE,"E46.1.0.0")}),-1.0]])]});
            var Q6;
            Q6=makeQuery(id+"F14.imprint","IMPRINT",FACE,{"disambiguationData":[TD([[makeQuery(id+"F14.imprint","IMPRINT",EDGE,{"derivedFrom":sQuery(id+"F14.wireOp",EDGE,"E44.bottom")}),1.0]])]});
            var Q7;
            Q7=makeQuery(id+"F14.imprint","IMPRINT",FACE,{"disambiguationData":[TD([[makeQuery(id+"F14.imprint","IMPRINT",EDGE,{"derivedFrom":sQuery(id+"F14.wireOp",EDGE,"E45.1.0.0")}),1.0]])]});
            var Q8;
            Q8=makeQuery(id+"F14.imprint","IMPRINT",FACE,{"disambiguationData":[TD([[makeQuery(id+"F14.imprint","IMPRINT",EDGE,{"derivedFrom":sQuery(id+"F14.wireOp",EDGE,"E45.2.0.0")}),1.0]])]});
            var Q9;
            Q9=makeQuery(id+"F14.imprint","IMPRINT",FACE,{"disambiguationData":[TD([[makeQuery(id+"F14.imprint","IMPRINT",EDGE,{"derivedFrom":sQuery(id+"F14.wireOp",EDGE,"E45.3.0.0")}),1.0]])]});
            var Q10;
            Q10=makeQuery(id+"F14.imprint","IMPRINT",FACE,{"disambiguationData":[TD([[makeQuery(id+"F14.imprint","IMPRINT",EDGE,{"derivedFrom":sQuery(id+"F14.wireOp",EDGE,"E45.4.0.0")}),1.0]])]});
            var Q11;
            Q11=makeQuery(id+"F14.imprint","IMPRINT",FACE,{"disambiguationData":[TD([[makeQuery(id+"F14.imprint","IMPRINT",EDGE,{"derivedFrom":sQuery(id+"F14.wireOp",EDGE,"E45.5.0.0")}),1.0]])]});
            var Q12;
            Q12=makeQuery(id+"F14.imprint","IMPRINT",FACE,{"disambiguationData":[TD([[makeQuery(id+"F14.imprint","IMPRINT",EDGE,{"derivedFrom":sQuery(id+"F14.wireOp",EDGE,"E45.6.0.0")}),1.0]])]});
            var Q13;
            Q13=makeQuery(id+"F14.imprint","IMPRINT",FACE,{"disambiguationData":[TD([[makeQuery(id+"F14.imprint","IMPRINT",EDGE,{"derivedFrom":sQuery(id+"F14.wireOp",EDGE,"E45.7.0.0")}),1.0]])]});
            var Q14;
            Q14=makeQuery(id+"F14.imprint","IMPRINT",FACE,{"disambiguationData":[TD([[makeQuery(id+"F14.imprint","IMPRINT",EDGE,{"derivedFrom":sQuery(id+"F14.wireOp",EDGE,"E96.MirrorCS")}),-1.0]])]});
            var Q15;
            Q15=makeQuery(id+"F14.imprint","IMPRINT",FACE,{"disambiguationData":[TD([[makeQuery(id+"F14.imprint","IMPRINT",EDGE,{"derivedFrom":sQuery(id+"F14.wireOp",EDGE,"E95.MirrorCS")}),-1.0]])]});
            var Q16;
            Q16=makeQuery(id+"F14.imprint","IMPRINT",FACE,{"disambiguationData":[TD([[makeQuery(id+"F14.imprint","IMPRINT",EDGE,{"derivedFrom":sQuery(id+"F14.wireOp",EDGE,"E101.MirrorCS")}),-1.0]])]});
            var Q17;
            Q17=makeQuery(id+"F14.imprint","IMPRINT",FACE,{"disambiguationData":[TD([[makeQuery(id+"F14.imprint","IMPRINT",EDGE,{"derivedFrom":sQuery(id+"F14.wireOp",EDGE,"E94.MirrorCS")}),1.0]])]});
            var Q18;
            Q18=makeQuery(id+"F14.imprint","IMPRINT",FACE,{"disambiguationData":[TD([[makeQuery(id+"F14.imprint","IMPRINT",EDGE,{"derivedFrom":sQuery(id+"F14.wireOp",EDGE,"E83.MirrorCS")}),-1.0]])]});
            var Q19;
            Q19=makeQuery(id+"F14.imprint","IMPRINT",FACE,{"disambiguationData":[TD([[makeQuery(id+"F14.imprint","IMPRINT",EDGE,{"derivedFrom":sQuery(id+"F14.wireOp",EDGE,"E82.MirrorCS")}),-1.0]])]});
            var Q20;
            Q20=makeQuery(id+"F14.imprint","IMPRINT",FACE,{"disambiguationData":[TD([[makeQuery(id+"F14.imprint","IMPRINT",EDGE,{"derivedFrom":sQuery(id+"F14.wireOp",EDGE,"E86.MirrorCS")}),1.0]])]});
            var Q21;
            Q21=makeQuery(id+"F14.imprint","IMPRINT",FACE,{"disambiguationData":[TD([[makeQuery(id+"F14.imprint","IMPRINT",EDGE,{"derivedFrom":sQuery(id+"F14.wireOp",EDGE,"E78.MirrorCS")}),-1.0]])]});
            var Q22;
            Q22=makeQuery(id+"F14.imprint","IMPRINT",FACE,{"disambiguationData":[TD([[makeQuery(id+"F14.imprint","IMPRINT",EDGE,{"derivedFrom":sQuery(id+"F14.wireOp",EDGE,"E73.MirrorCS")}),1.0]])]});
            var Q23;
            Q23=makeQuery(id+"F14.imprint","IMPRINT",FACE,{"disambiguationData":[TD([[makeQuery(id+"F14.imprint","IMPRINT",EDGE,{"derivedFrom":sQuery(id+"F14.wireOp",EDGE,"E69.MirrorCS")}),1.0]])]});
            var Q24;
            Q24=makeQuery(id+"F14.imprint","IMPRINT",FACE,{"disambiguationData":[TD([[makeQuery(id+"F14.imprint","IMPRINT",EDGE,{"derivedFrom":sQuery(id+"F14.wireOp",EDGE,"E65.MirrorCS")}),-1.0]])]});
            var Q25;
            Q25=makeQuery(id+"F14.imprint","IMPRINT",FACE,{"disambiguationData":[TD([[makeQuery(id+"F14.imprint","IMPRINT",EDGE,{"derivedFrom":sQuery(id+"F14.wireOp",EDGE,"E61.MirrorCS")}),-1.0]])]});
            var Q26;
            Q26=makeQuery(id+"F14.imprint","IMPRINT",FACE,{"disambiguationData":[TD([[makeQuery(id+"F14.imprint","IMPRINT",EDGE,{"derivedFrom":sQuery(id+"F14.wireOp",EDGE,"E57.MirrorCS")}),-1.0]])]});
            var Q27;
            Q27=makeQuery(id+"F14.imprint","IMPRINT",FACE,{"disambiguationData":[TD([[makeQuery(id+"F14.imprint","IMPRINT",EDGE,{"derivedFrom":sQuery(id+"F14.wireOp",EDGE,"E53.MirrorCS")}),1.0]])]});
            extrude(context, id + "F15", {"entities" : qUnion([Q0, Q1, Q2, Q3, Q4, Q5, Q6, Q7, Q8, Q9, Q10, Q11, Q12, Q13, Q14, Q15, Q16, Q17, Q18, Q19, Q20, Q21, Q22, Q23, Q24, Q25, Q26, Q27]), "operationType" : NewBodyOperationType.REMOVE, "oppositeDirection" : true, "depth" : 3 * mm});
        }
    });
